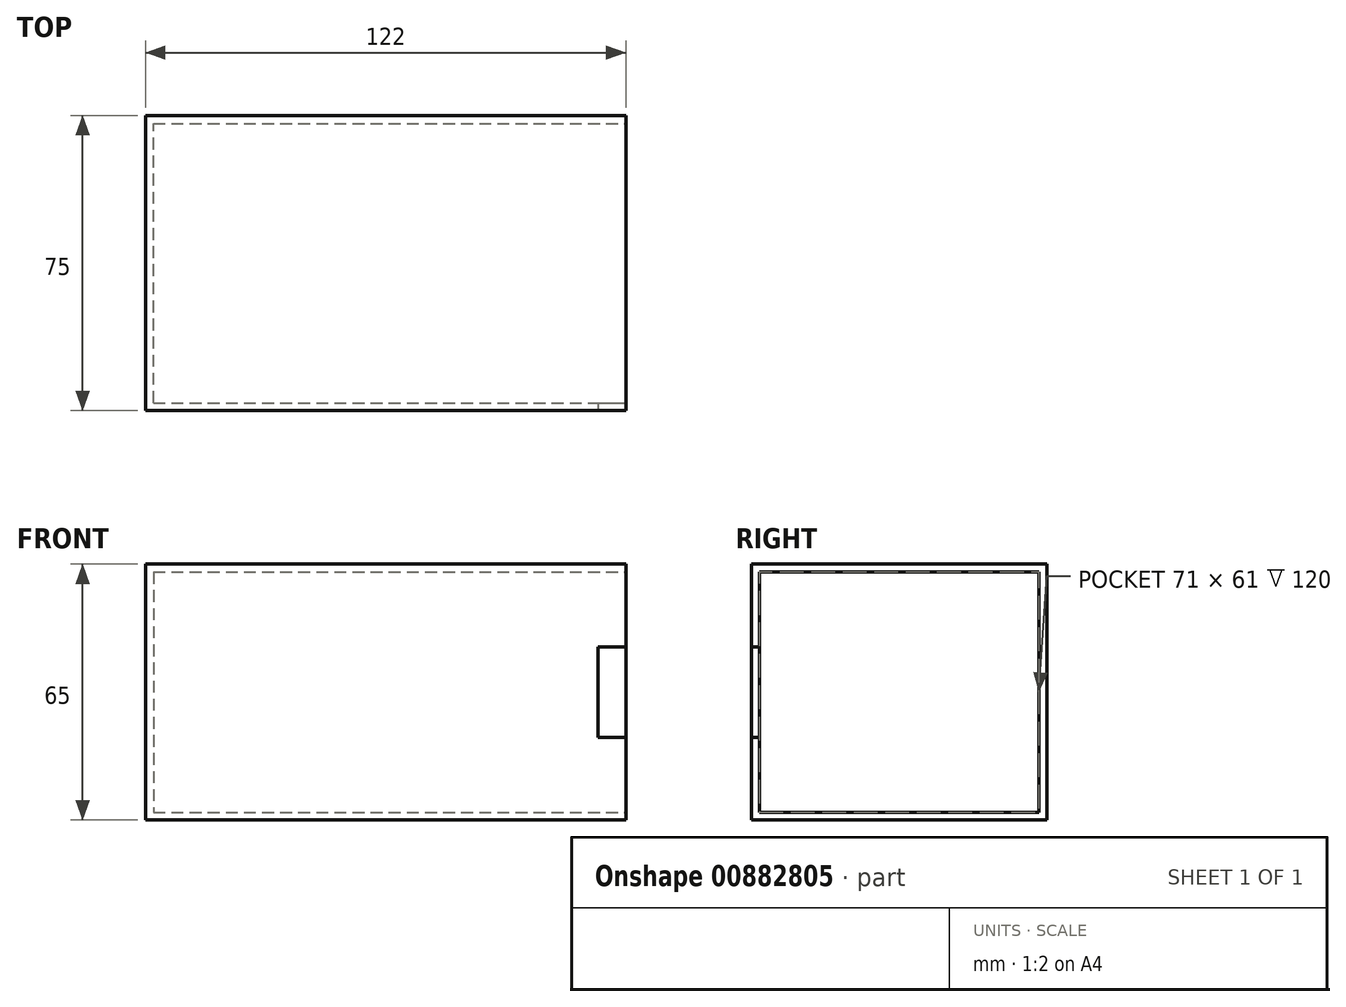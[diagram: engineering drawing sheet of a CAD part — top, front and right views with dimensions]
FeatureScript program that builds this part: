
annotation { "Feature Type Name" : "Feature", "Feature Type Description" : "" }
export const myFeature = defineFeature(function(context is Context, id is Id, definition is map)
    precondition{}
    {
        {
            var Q0;
            Q0=qCreatedBy(makeId("Top.planeOp"),FACE);
            var sketch = newSketch(context, id + "F0", { "sketchPlane" : qUnion([Q0])});
            skLineSegment(sketch, "E0.bottom", {"start": v(0, 0) * mm, "end": v(122, 0) * mm});
            skLineSegment(sketch, "E0.top", {"start": v(0, 75) * mm, "end": v(122, 75) * mm});
            skLineSegment(sketch, "E0.left", {"start": v(0, 0) * mm, "end": v(0, 75) * mm});
            skLineSegment(sketch, "E0.right", {"start": v(122, 0) * mm, "end": v(122, 75) * mm});
            skSolve(sketch);
        }
        {
            var Q0;
            Q0 = qSketchRegion(id + "F0", true);
            var Q1;
            Q1=makeQuery(id+"F0.imprint","IMPRINT",FACE,{"disambiguationData":[TD([[makeQuery(id+"F0.imprint","IMPRINT",EDGE,{"derivedFrom":sQuery(id+"F0.wireOp",EDGE,"E0.bottom")}),1.0]])]});
            extrude(context, id + "F1", {"entities" : qUnion([Q0, Q1]), "depth" : 65 * mm, "offsetDistance" : 25 * mm});
        }
        {
            var Q0;
            Q0=makeQuery(id+"F1.opExtrude","SWEPT_FACE",FACE,{"disambiguationData":[OSD([sQuery(id+"F0.wireOp",EDGE,"E0.right")])]});
            var sketch = newSketch(context, id + "F2", { "sketchPlane" : qUnion([Q0])});
            skLineSegment(sketch, "E1.bottom", {"start": v(2, 63) * mm, "end": v(73, 63) * mm});
            skLineSegment(sketch, "E1.top", {"start": v(2, 2) * mm, "end": v(73, 2) * mm});
            skLineSegment(sketch, "E1.left", {"start": v(2, 63) * mm, "end": v(2, 2) * mm});
            skLineSegment(sketch, "E1.right", {"start": v(73, 63) * mm, "end": v(73, 2) * mm});
            skSolve(sketch);
        }
        {
            var Q0;
            Q0 = qSketchRegion(id + "F2", true);
            extrude(context, id + "F3", {"entities" : qUnion([Q0]), "operationType" : NewBodyOperationType.REMOVE, "oppositeDirection" : true, "depth" : 120 * mm, "offsetDistance" : 25 * mm});
        }
        {
            var Q0;
            Q0=makeQuery(id+"F1.opExtrude","SWEPT_FACE",FACE,{"disambiguationData":[OSD([sQuery(id+"F0.wireOp",EDGE,"E0.bottom")])]});
            var sketch = newSketch(context, id + "F4", { "sketchPlane" : qUnion([Q0])});
            skLineSegment(sketch, "E2.bottom", {"start": v(115, 44) * mm, "end": v(122, 44) * mm});
            skLineSegment(sketch, "E2.top", {"start": v(115, 21) * mm, "end": v(122, 21) * mm});
            skLineSegment(sketch, "E2.left", {"start": v(115, 44) * mm, "end": v(115, 21) * mm});
            skLineSegment(sketch, "E2.right", {"start": v(122, 44) * mm, "end": v(122, 21) * mm});
            skSolve(sketch);
        }
        {
            var Q0;
            Q0 = qSketchRegion(id + "F4", true);
            extrude(context, id + "F5", {"entities" : qUnion([Q0]), "operationType" : NewBodyOperationType.REMOVE, "oppositeDirection" : true, "depth" : 25 * mm, "offsetDistance" : 25 * mm});
        }
    });
